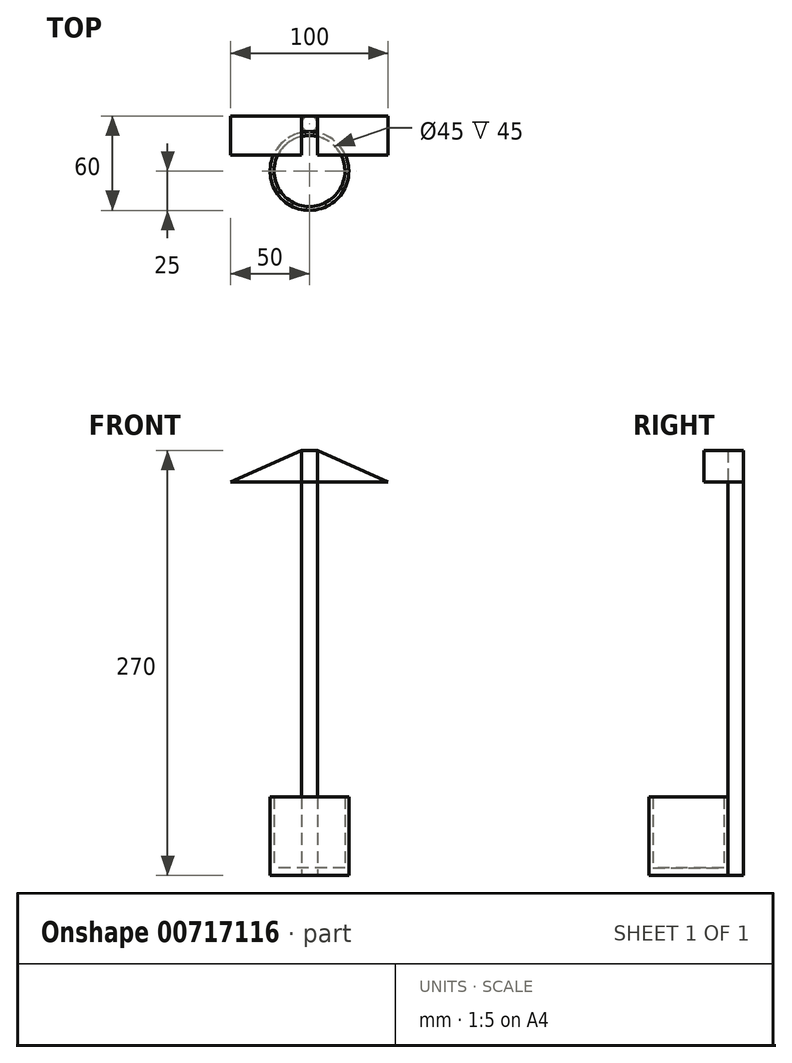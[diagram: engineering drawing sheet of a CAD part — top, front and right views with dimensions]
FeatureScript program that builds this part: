
annotation { "Feature Type Name" : "Feature", "Feature Type Description" : "" }
export const myFeature = defineFeature(function(context is Context, id is Id, definition is map)
    precondition{}
    {
        {
            var Q0;
            Q0=qCreatedBy(makeId("Top.planeOp"),FACE);
            var sketch = newSketch(context, id + "F0", { "sketchPlane" : qUnion([Q0])});
            skCircle(sketch, "E0", {"center": v(0, 0) * mm, "radius": 25 * mm});
            skCircle(sketch, "E1", {"center": v(0, 30) * mm, "radius": 5 * mm});
            skCircle(sketch, "E2", {"center": v(0, 0) * mm, "radius": 22.5 * mm});
            skSolve(sketch);
        }
        {
            var Q0;
            Q0=makeQuery(id+"F0.imprint","IMPRINT",FACE,{"disambiguationData":[TD([[makeQuery(id+"F0.imprint","IMPRINT",EDGE,{"derivedFrom":sQuery(id+"F0.wireOp",EDGE,"E0")}),1.0]])]});
            extrude(context, id + "F1", {"entities" : qUnion([Q0]), "depth" : 50 * mm, "offsetDistance" : 25 * mm});
        }
        {
            var Q0;
            Q0=makeQuery(id+"F0.imprint","IMPRINT",FACE,{"disambiguationData":[TD([[makeQuery(id+"F0.imprint","IMPRINT",EDGE,{"derivedFrom":sQuery(id+"F0.wireOp",EDGE,"E1")}),1.0]])]});
            extrude(context, id + "F2", {"entities" : qUnion([Q0]), "operationType" : NewBodyOperationType.ADD, "depth" : 250 * mm, "offsetDistance" : 25 * mm});
        }
        {
            var Q0;
            Q0=makeQuery(id+"F0.imprint","IMPRINT",FACE,{"disambiguationData":[TD([[makeQuery(id+"F0.imprint","IMPRINT",EDGE,{"derivedFrom":sQuery(id+"F0.wireOp",EDGE,"E2")}),1.0]])]});
            extrude(context, id + "F3", {"entities" : qUnion([Q0]), "operationType" : NewBodyOperationType.ADD, "depth" : 5 * mm, "offsetDistance" : 25 * mm});
        }
        {
            var Q0;
            Q0=makeQuery(id+"F2.opExtrude","CAP_FACE",FACE,{"disambiguationData":[OSD([sQuery(id+"F0.wireOp",EDGE,"E1")])],"isStart":false});
            var sketch = newSketch(context, id + "F4", { "sketchPlane" : qUnion([Q0])});
            skLineSegment(sketch, "E3.bottom", {"start": v(-5, 35) * mm, "end": v(5, 35) * mm});
            skLineSegment(sketch, "E3.top", {"start": v(-5, 25) * mm, "end": v(5, 25) * mm});
            skLineSegment(sketch, "E3.left", {"start": v(-5, 35) * mm, "end": v(-5, 25) * mm});
            skLineSegment(sketch, "E3.right", {"start": v(5, 35) * mm, "end": v(5, 25) * mm});
            skSolve(sketch);
        }
        {
            var Q0;
            {var subQ0=sQuery(id+"F4.wireOp",EDGE,"E3.left");var subQ1=sQuery(id+"F4.wireOp",EDGE,"E3.bottom");var subQ2=makeQuery(id+"F4.imprint","INTERSECT",VERTEX,{"derivedFrom":[subQ1,subQ0]});Q0=makeQuery(id+"F4.imprint","IMPRINT",FACE,{"disambiguationData":[TD([[makeQuery(id+"F4.imprint","IMPRINT",EDGE,{"disambiguationData":[TD([[subQ2,-1.0]])],"derivedFrom":subQ1}),-1.0]])]});}
            var Q1;
            {var subQ0=makeQuery(id+"F2.opExtrude","CAP_EDGE",EDGE,{"disambiguationData":[OSD([sQuery(id+"F0.wireOp",EDGE,"E1")])],"isStart":false});var subQ1=makeQuery(id+"F4.imprint","INTERSECT",VERTEX,{"derivedFrom":[subQ0,sQuery(id+"F4.wireOp",EDGE,"E3.bottom")]});Q1=makeQuery(id+"F4.imprint","IMPRINT",FACE,{"disambiguationData":[TD([[makeQuery(id+"F4.imprint","IMPRINT",EDGE,{"disambiguationData":[TD([[subQ1,-1.0]])],"derivedFrom":subQ0}),1.0]])]});}
            var Q2;
            {var subQ0=sQuery(id+"F4.wireOp",EDGE,"E3.right");var subQ1=sQuery(id+"F4.wireOp",EDGE,"E3.bottom");var subQ2=makeQuery(id+"F4.imprint","INTERSECT",VERTEX,{"derivedFrom":[subQ1,subQ0]});Q2=makeQuery(id+"F4.imprint","IMPRINT",FACE,{"disambiguationData":[TD([[makeQuery(id+"F4.imprint","IMPRINT",EDGE,{"disambiguationData":[TD([[subQ2,1.0]])],"derivedFrom":subQ1}),-1.0]])]});}
            var Q3;
            {var subQ0=sQuery(id+"F4.wireOp",EDGE,"E3.right");var subQ1=sQuery(id+"F4.wireOp",EDGE,"E3.top");var subQ2=makeQuery(id+"F4.imprint","INTERSECT",VERTEX,{"derivedFrom":[subQ1,subQ0]});Q3=makeQuery(id+"F4.imprint","IMPRINT",FACE,{"disambiguationData":[TD([[makeQuery(id+"F4.imprint","IMPRINT",EDGE,{"disambiguationData":[TD([[subQ2,1.0]])],"derivedFrom":subQ1}),1.0]])]});}
            var Q4;
            {var subQ0=sQuery(id+"F4.wireOp",EDGE,"E3.left");var subQ1=sQuery(id+"F4.wireOp",EDGE,"E3.top");var subQ2=makeQuery(id+"F4.imprint","INTERSECT",VERTEX,{"derivedFrom":[subQ1,subQ0]});Q4=makeQuery(id+"F4.imprint","IMPRINT",FACE,{"disambiguationData":[TD([[makeQuery(id+"F4.imprint","IMPRINT",EDGE,{"disambiguationData":[TD([[subQ2,-1.0]])],"derivedFrom":subQ1}),1.0]])]});}
            extrude(context, id + "F5", {"entities" : qUnion([Q0, Q1, Q2, Q3, Q4]), "operationType" : NewBodyOperationType.ADD, "depth" : 20 * mm, "offsetDistance" : 25 * mm});
        }
        {
            var Q0;
            Q0=makeQuery(id+"F5.opExtrude","SWEPT_FACE",FACE,{"disambiguationData":[OSD([sQuery(id+"F4.wireOp",EDGE,"E3.bottom")])]});
            var sketch = newSketch(context, id + "F6", { "sketchPlane" : qUnion([Q0])});
            skLineSegment(sketch, "E4", {"start": v(0, 250) * mm, "end": v(-50, 250) * mm});
            skLineSegment(sketch, "E5", {"start": v(-50, 250) * mm, "end": v(-5, 270) * mm});
            skLineSegment(sketch, "E6", {"start": v(0, 250) * mm, "end": v(50, 250) * mm});
            skLineSegment(sketch, "E7", {"start": v(50, 250) * mm, "end": v(5, 270) * mm});
            skLineSegment(sketch, "E8", {"start": v(0, 250) * mm, "end": v(0, 301.2) * mm});
            skLineSegment(sketch, "E9", {"start": v(-50, 250) * mm, "end": v(31.76, 286.34) * mm});
            skLineSegment(sketch, "E10", {"start": v(50, 250) * mm, "end": v(-21.15, 281.62) * mm});
            skSolve(sketch);
        }
        {
            var Q0;
            {var subQ1=sQuery(id+"F4.wireOp",EDGE,"E3.bottom");var subQ2=makeQuery(id+"F5.opExtrude","SWEPT_EDGE",EDGE,{"disambiguationData":[OSD([subQ1,sQuery(id+"F4.wireOp",EDGE,"E3.left")])]});Q0=makeQuery(id+"F6.imprint","IMPRINT",FACE,{"disambiguationData":[TD([[makeQuery(id+"F6.imprint","IMPRINT",EDGE,{"derivedFrom":subQ2}),1.0]])]});}
            var Q1;
            {var subQ1=sQuery(id+"F4.wireOp",EDGE,"E3.bottom");var subQ2=makeQuery(id+"F5.opExtrude","SWEPT_EDGE",EDGE,{"disambiguationData":[OSD([subQ1,sQuery(id+"F4.wireOp",EDGE,"E3.right")])]});Q1=makeQuery(id+"F6.imprint","IMPRINT",FACE,{"disambiguationData":[TD([[makeQuery(id+"F6.imprint","IMPRINT",EDGE,{"derivedFrom":subQ2}),-1.0]])]});}
            extrude(context, id + "F7", {"entities" : qUnion([Q0, Q1]), "oppositeDirection" : true, "depth" : 25 * mm, "offsetDistance" : 25 * mm});
        }
    });
